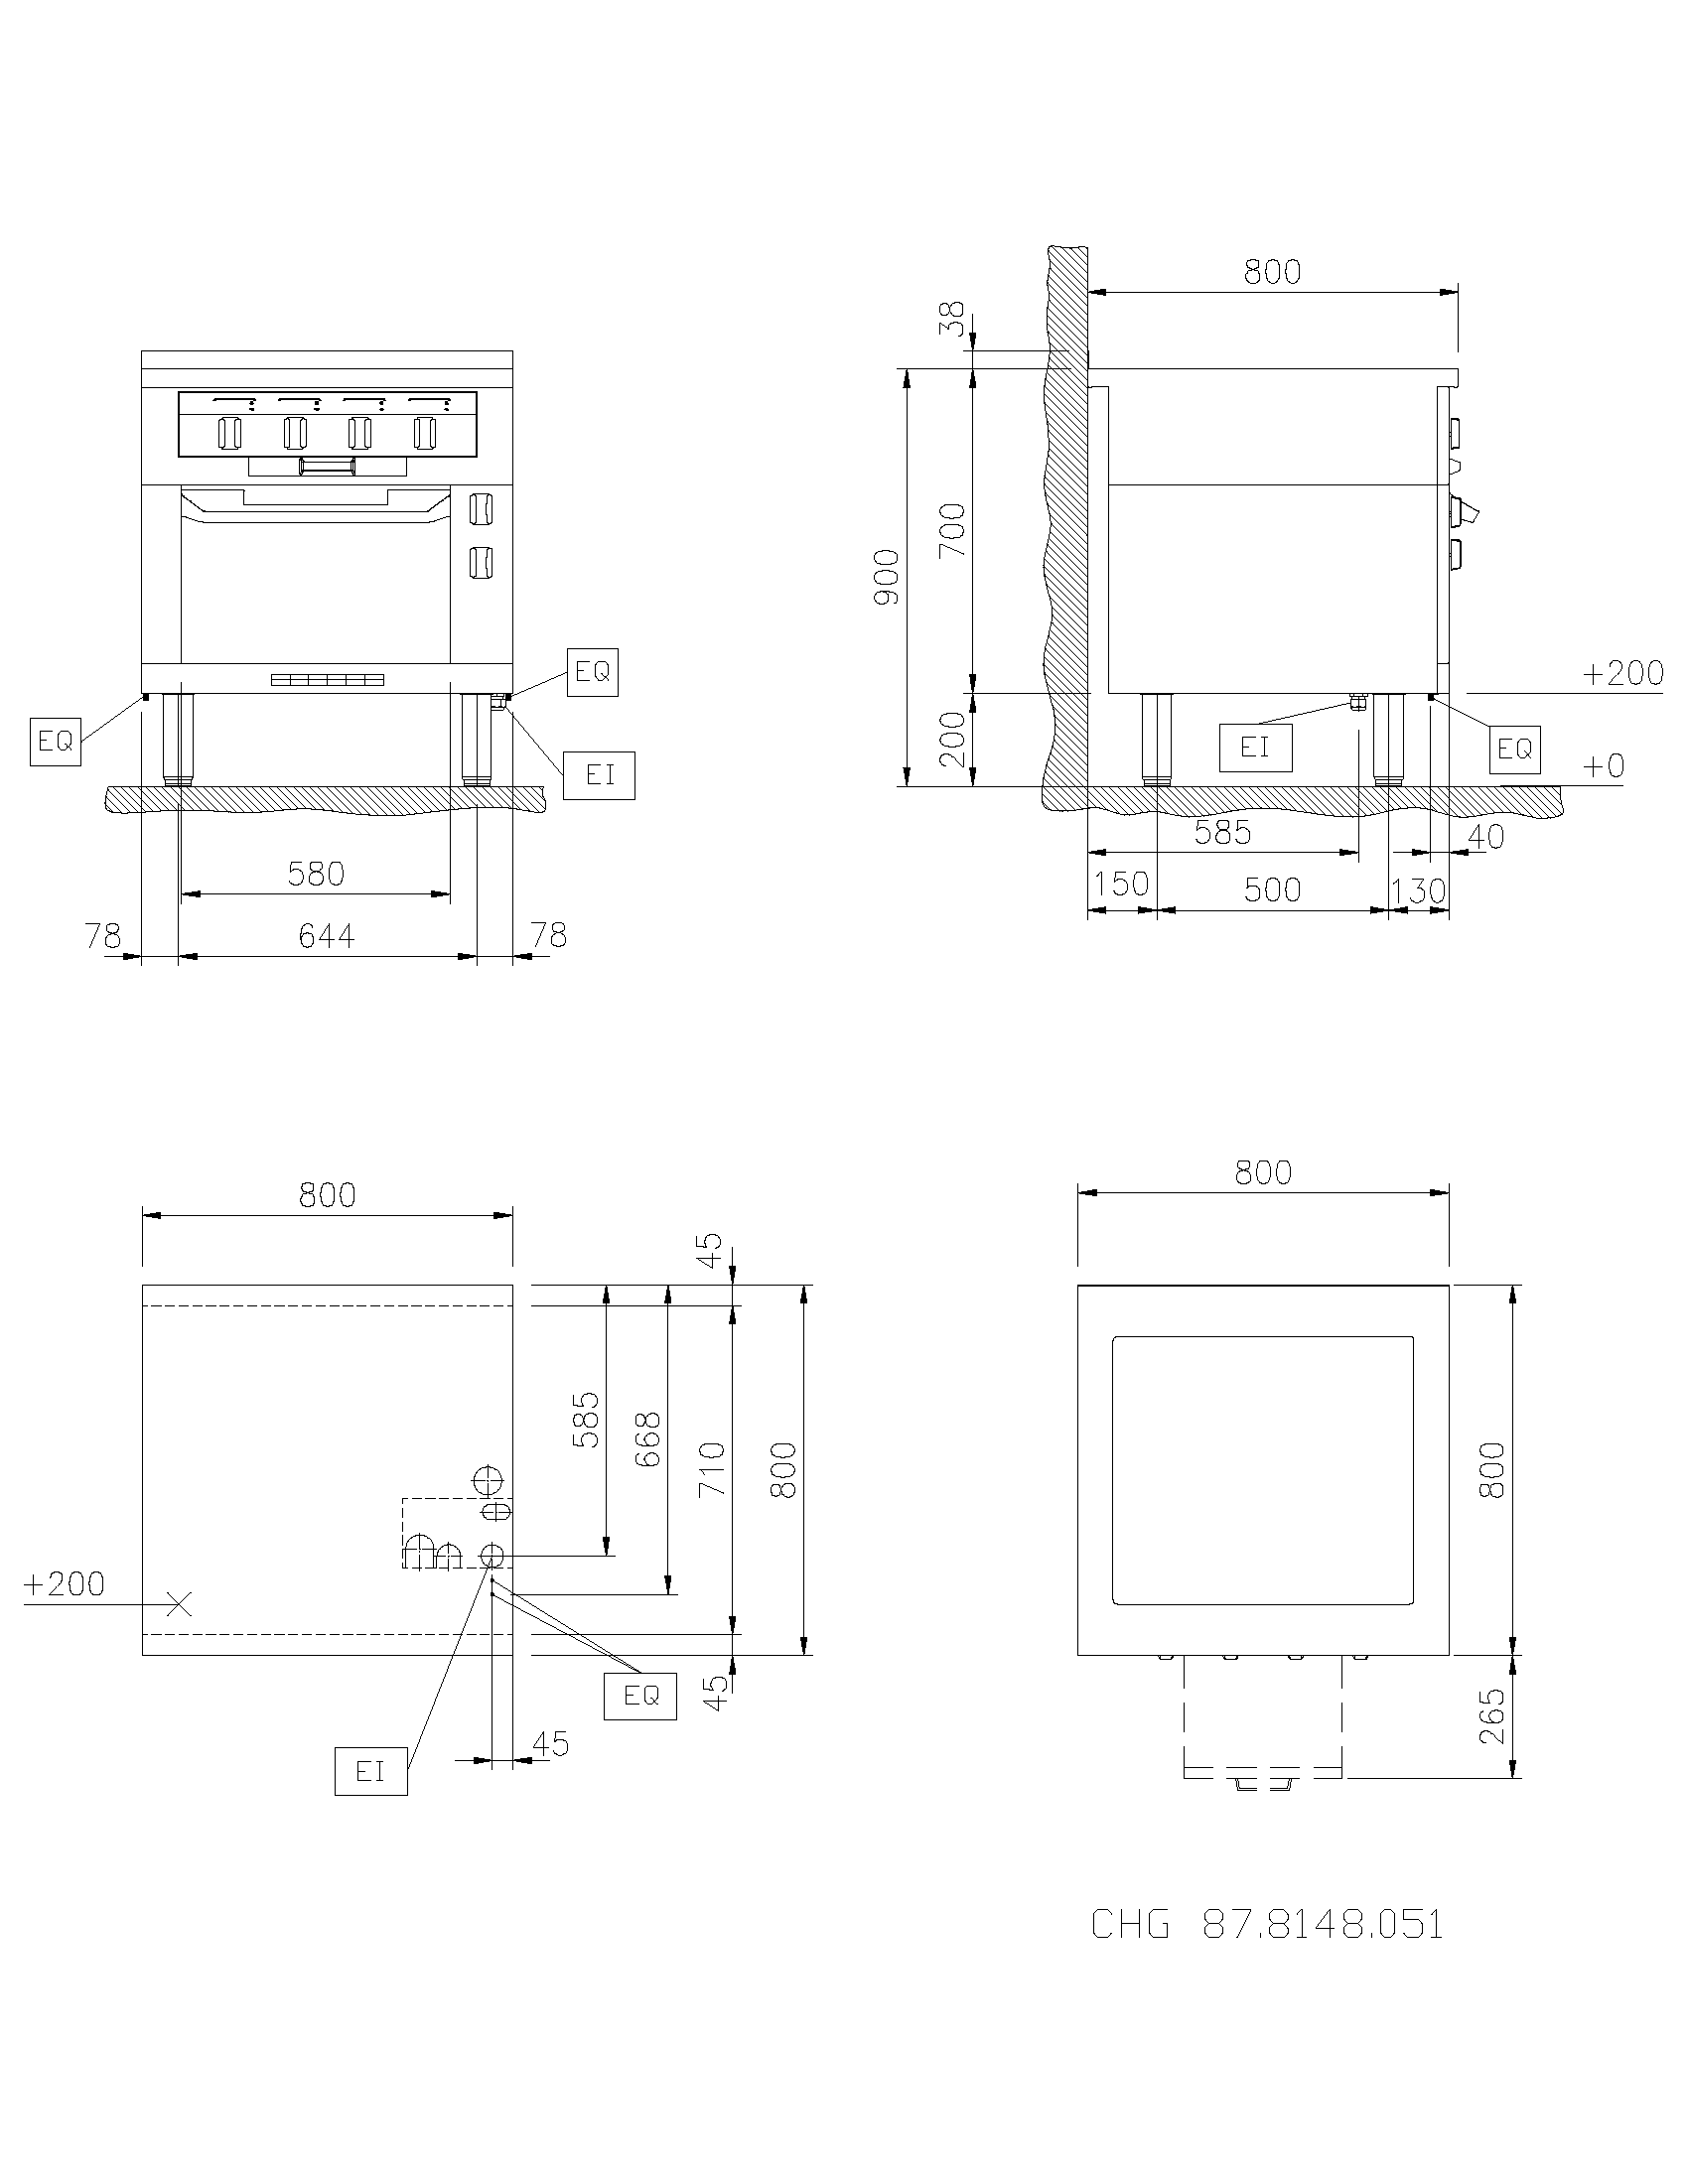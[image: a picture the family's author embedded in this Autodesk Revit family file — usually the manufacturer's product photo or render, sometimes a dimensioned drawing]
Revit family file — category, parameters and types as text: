
# Revit family: QF_ELECTROLUXPROFESSIONAL_588429_MAINECH8AO
name_source: partatom
category: Attrezzature speciali
units: mm (PartAtom-declared; Revit-internal decimal feet)

## family parameters
Basato su piano di lavoro = No
Condiviso = No
Punto di calcolo locali = No
Quota connettore circolare = Usa diametro
Sempre verticale = Sì
Taglio con vuoti quando caricato = No
Tipo di parte = Normale

## types (1)
- Standard
    Accessory = Sì
    Cold Water Size = 0"
    Compressed Air Pressure = 0.00 psi
    Compressed Air Size = 0"
    Compressed Air Volume = 0 GPM
    Condensate Return Size = 0"
    Cycle = 50 Hz
    Depth Actual = 800 mm  [stored 2.62467 ft]
    Descrizione = INDUCTION,4Z,ST.OVEN PASS,2S,800X800X700
    Direct Waste Size = 0"
    Gas Input Pressure = 0.0
    Gas KW = 0
    Gas Size = 0"
    HP = 33.9 HP
    Height Actual = 700 mm  [stored 2.29659 ft]
    Hot Water Size = 0"
    Item Number = 588429
    Length Actual = 800 mm  [stored 2.62467 ft]
    Modello = MAINECH8AO
    Phase = 3
    Produttore = Electrolux Professional
    Prospetto di default = 0 mm  [stored 0 ft]
    Refrigerant Compressor Remote = Sì
    Refrigeration Liquid Line Size = 0 mm  [stored 0 ft]
    Refrigeration Suction Line Size = 0 mm  [stored 0 ft]
    Steam Consumption per Hour = 0
    Steam Supply Maximum Pressure = 0.00 psi
    Steam Supply Minimum Pressure = 0.00 psi
    Steam Supply Size = 0"
    URL = https://www.electroluxprofessional.com
    URL Manufacturer = https://www.electroluxprofessional.com
    Volts = 400 V
    Watts = 25300 W
    Weight = 125.00 kg

note: source unit labels omitted for Gas Input Pressure — the stored unit's dimension contradicts the parameter name (converter mislabeling)

note: [stored X ft] marks values corroborated as IEEE doubles in the binary element streams (Revit-internal decimal feet)

## geometry (parser evidence)
native form markers: Blend x24, Sweep x10
no freeform markers — native parametric forms only
